# Revit family: 44280170
name_source: partatom
category: Plumbing Fixtures
revit_build: Autodesk Revit 2016 (Build: 20150714_1515(x64)
units: mm (PartAtom-declared; Revit-internal decimal feet)

## family parameters
Always vertical = Yes
Cut with Voids When Loaded = No
OmniClass Number = 23.45.55.00
OmniClass Title = Sanitary Faucets, Wastes
Part Type = Normal
Room Calculation Point = No
Round Connector Dimension = Use Diameter
Shared = No
Work Plane-Based = No

## types (1)
- 44280170 Hand shower, d 100 mm
    2D/3D/BIM Files URL = http://static.hansa.com
    Advanced Features = Limescale Protection Technology
    Approval ABP = P-IX 28552/IIA
    AssetType = Fixed
    BIMObjectName = 44280170
    BodyMaterial = Brass
    Brand = Hansa
    Catalog Drawing URL = http://static.hansa.com
    Category = Health care, shower
    CloseOffRating = 0
    Color = Chrome
    Connection Size = G1/2
    ConvergoRefNr = 0087-1803-0061-FI
    Customs Code = 39249000
    Diameter = 100 mm  [stored 0.328084 ft]
    Dimension Drawing URL = http://static.hansa.com
    DurationUnit = Year
    EAN Number = 4015474268449
    EN Standard = EN 1112
    FDV Document URL = http://www.hansa.com
    FaucetMainMaterial = Brass
    Finish = Polished
    Flow Drawing URL = http://static.hansa.com
    Flow Rate At 300kPa = 0.2 L/s
    FlowCoefficient = 0
    Group = Hand shower
    Hand Shower = Hand shower for hospitals
    Hand Shower Size = Ø 100 mm
    IfcExportAs = IfcValveType
    IfcExportType = FAUCET
    Installation and Maintenance = http://static.hansa.com
    Long Marketing = HANSAMEDIPRO FLEX innovative handshower with ergonomic handle.
    ManufacterURL = http://www.hansa.com
    Manufacturer = Hansa
    ManufacturerName = Hansa
    Market = AUT;BEL;CZE;DEU;ESP;FRA;INT;ITA;NLD;SVK
    Material = Brass & plastic
    Max. Hot Water Supply = 65 °C
    Mechanical Parts = Litter filter(s)
    Model = 44280170 Hand shower, d 100 mm
    ModelReference = 44280170
    NBSDescription = Shower heads
    NBSReference = 45-35-70/333
    NRF Number = 4202976
    Name = 44280170 Hand shower, d 100 mm
    Name_en = 44280170 Hand shower, d 100 mm
    NominalDepth = 90 mm
    NominalHeight = 146 mm  [stored 0.479003 ft]
    NominalWidth = 100 mm  [stored 0.328084 ft]
    Package Weight = 0.26 kg
    Package external Dimensions = 158 x 103 x 86
    Product Code = 44280170
    Product Datasheet = http://www.hansa.com
    Product Family = Hansademipro Flex
    Product Image URL = http://static.hansa.com
    Product URL = http://static.hansa.com
    RSK Number = 8377532
    Revision = 2
    Safety Sales Arguments = THERMO COOL. Improved safety – the housing of the fittings conducts minimal heat.
    Shape = Sculptured
    Shower Spray = Low aerosol
    Shower Spray Number = 1 spray
    Size = 100x89.5x146 mm
    Spare Parts = http://static.hansa.com
    URL ABP = http://static.hansa.com
    Uniclass2 = Pr_40_30_96_76
    Uniclass2015Description = Shower heads
    Uniclass2015Reference = Pr_40_20_87_76
    Usage Group = Health centers, hospitals
    Version = 2
    VersionDate = 01/01/2019
    WarrantyDescription = http://warranty.hansa.com
    WarrantyDurationUnit = Year
    WorkingPressure = 50 - 500 kPa

note: [stored X ft] marks values corroborated as IEEE doubles in the binary element streams (Revit-internal decimal feet)

## geometry (parser evidence)
native form markers: Sweep x3
no freeform markers — native parametric forms only
